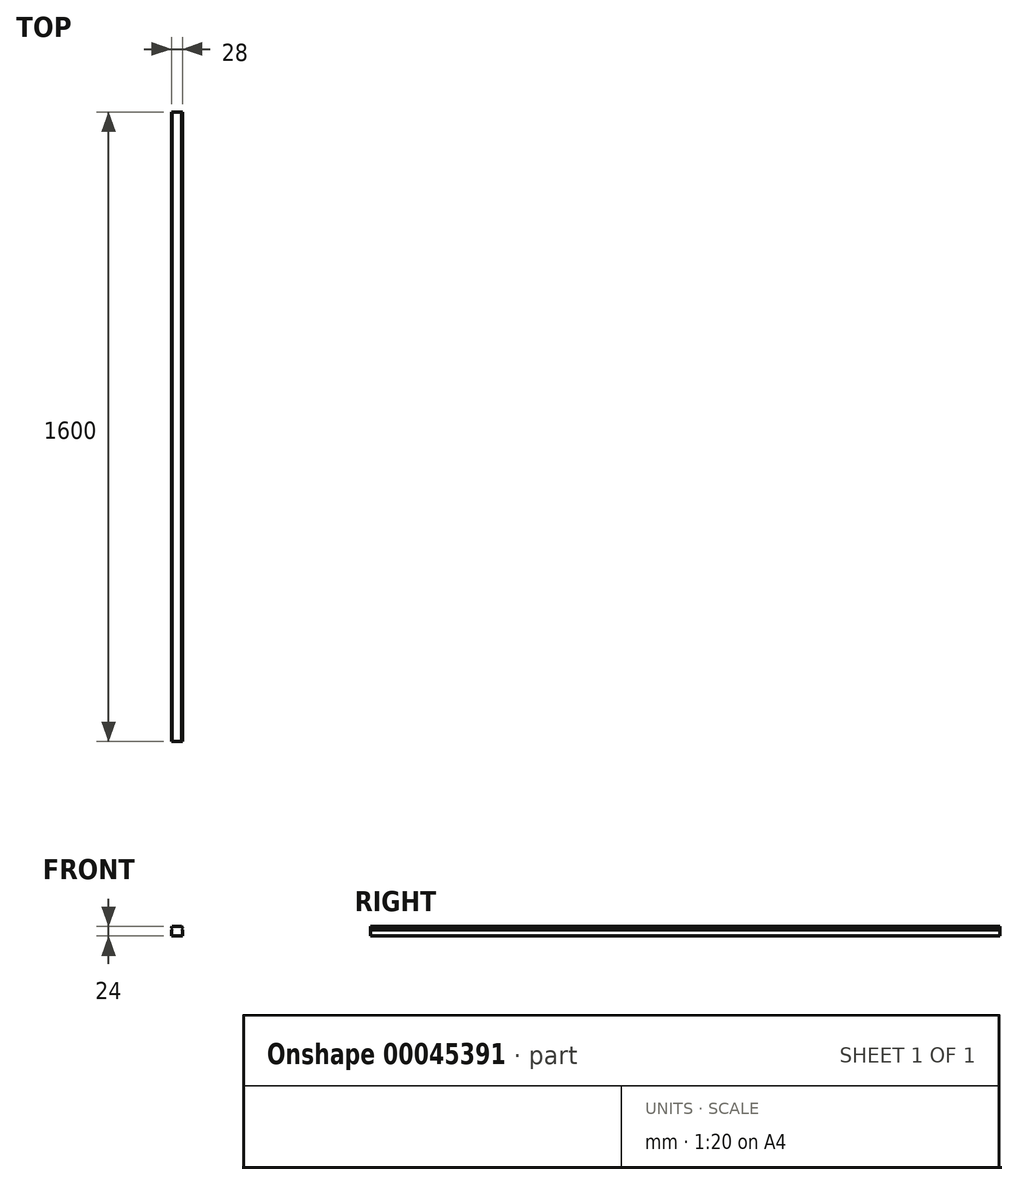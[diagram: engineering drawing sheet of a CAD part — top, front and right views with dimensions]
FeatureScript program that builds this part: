
annotation { "Feature Type Name" : "Feature", "Feature Type Description" : "" }
export const myFeature = defineFeature(function(context is Context, id is Id, definition is map)
    precondition{}
    {
        {
            var Q0;
            Q0=qCreatedBy(makeId("Front.planeOp"),FACE);
            var sketch = newSketch(context, id + "F0", { "sketchPlane" : qUnion([Q0])});
            skLineSegment(sketch, "E0.bottom", {"start": v(-9.9, 12.6) * mm, "end": v(13.87, 12.6) * mm});
            skLineSegment(sketch, "E0.top", {"start": v(-12.01, -11.4) * mm, "end": v(15.99, -11.4) * mm});
            skLineSegment(sketch, "E0.left", {"start": v(-12.01, 10.49) * mm, "end": v(-12.01, 9.49) * mm});
            skLineSegment(sketch, "E0.right", {"start": v(15.99, 10.49) * mm, "end": v(15.99, 9.49) * mm});
            skLineSegment(sketch, "E1", {"start": v(-9.9, 12.6) * mm, "end": v(-12.01, 10.49) * mm});
            skLineSegment(sketch, "E2", {"start": v(13.87, 12.6) * mm, "end": v(15.99, 10.49) * mm});
            skLineSegment(sketch, "E3", {"start": v(-12.01, 9.49) * mm, "end": v(-9.18, 6.66) * mm});
            skLineSegment(sketch, "E4", {"start": v(-9.18, 6.66) * mm, "end": v(-12.01, 3.83) * mm});
            skLineSegment(sketch, "E5", {"start": v(15.99, 9.49) * mm, "end": v(13.16, 6.66) * mm});
            skLineSegment(sketch, "E6", {"start": v(13.16, 6.66) * mm, "end": v(15.99, 3.83) * mm});
            skLineSegment(sketch, "E7.trimOffspring", {"start": v(-12.01, 3.83) * mm, "end": v(-12.01, -11.4) * mm});
            skLineSegment(sketch, "E8.trimOffspring", {"start": v(15.99, 3.83) * mm, "end": v(15.99, -11.4) * mm});
            skSolve(sketch);
        }
        {
            var Q0;
            Q0=qSketchRegion(id+"F0",true);
            extrude(context, id + "F1", {"entities" : qUnion([Q0]), "depth" : 1600 * mm});
        }
    });
